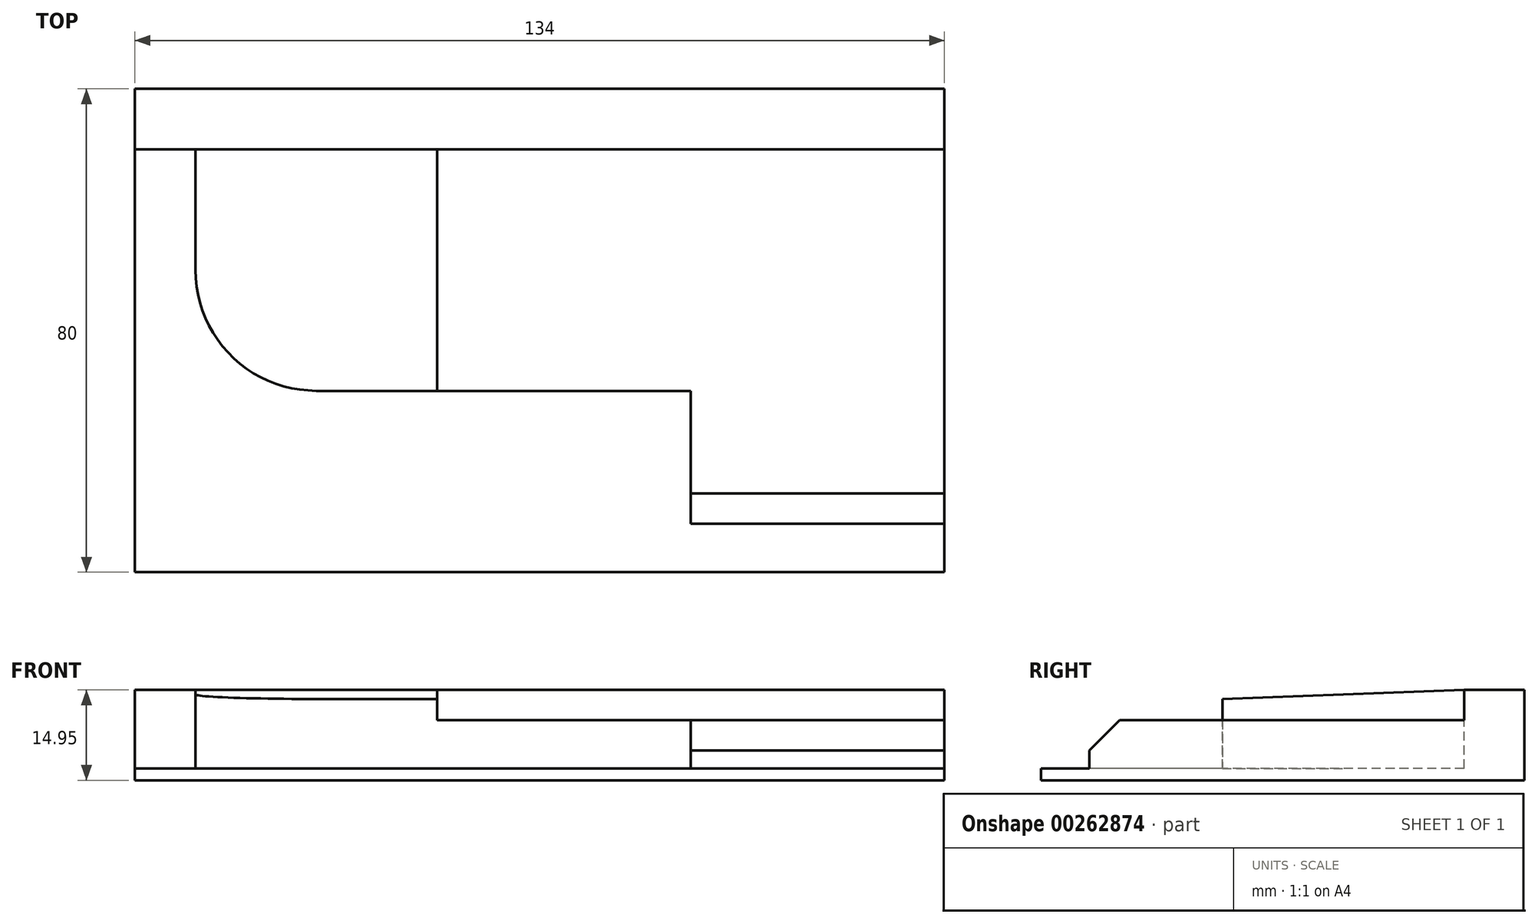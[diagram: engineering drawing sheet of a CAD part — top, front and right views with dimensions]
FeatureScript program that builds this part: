
annotation { "Feature Type Name" : "Feature", "Feature Type Description" : "" }
export const myFeature = defineFeature(function(context is Context, id is Id, definition is map)
    precondition{}
    {
        {
            var Q0;
            Q0=qCreatedBy(makeId("Right.planeOp"),FACE);
            var sketch = newSketch(context, id + "F0", { "sketchPlane" : qUnion([Q0])});
            skLineSegment(sketch, "E0", {"start": v(0, 0) * mm, "end": v(40, 0) * mm});
            skLineSegment(sketch, "E1", {"start": v(0, 0) * mm, "end": v(-40, 0) * mm});
            skLineSegment(sketch, "E2", {"start": v(40, 0) * mm, "end": v(40, 13) * mm});
            skLineSegment(sketch, "E3", {"start": v(40, 13) * mm, "end": v(30, 13) * mm});
            skLineSegment(sketch, "E4", {"start": v(30, 13) * mm, "end": v(30, 8) * mm});
            skLineSegment(sketch, "E5", {"start": v(30, 8) * mm, "end": v(-32, 8) * mm});
            skLineSegment(sketch, "E6", {"start": v(-32, 8) * mm, "end": v(-32, 0) * mm});
            skLineSegment(sketch, "E7", {"start": v(-40, 0) * mm, "end": v(-40, -1.95) * mm});
            skLineSegment(sketch, "E8", {"start": v(-40, -1.95) * mm, "end": v(40, -1.95) * mm});
            skLineSegment(sketch, "E9", {"start": v(40, -1.95) * mm, "end": v(40, 0) * mm});
            skSolve(sketch);
        }
        {
            var Q0;
            {var subQ3=sQuery(id+"F0.wireOp",EDGE,"E0");Q0=makeQuery(id+"F0.imprint","IMPRINT",FACE,{"disambiguationData":[TD([[makeQuery(id+"F0.imprint","IMPRINT",EDGE,{"derivedFrom":subQ3}),-1.0]])]});}
            var Q1;
            {var subQ1=sQuery(id+"F0.wireOp",EDGE,"E0");Q1=makeQuery(id+"F0.imprint","IMPRINT",FACE,{"disambiguationData":[TD([[makeQuery(id+"F0.imprint","IMPRINT",EDGE,{"derivedFrom":subQ1}),1.0]])]});}
            extrude(context, id + "F1", {"entities" : qUnion([Q0, Q1]), "depth" : 42 * mm, "symmetric" : true});
        }
        {
            var Q0;
            Q0=makeQuery(id+"F1.opExtrude","CAP_FACE",FACE,{"disambiguationData":[OSD([sQuery(id+"F0.wireOp",EDGE,"E1"),sQuery(id+"F0.wireOp",EDGE,"E2"),sQuery(id+"F0.wireOp",EDGE,"E3"),sQuery(id+"F0.wireOp",EDGE,"E4"),sQuery(id+"F0.wireOp",EDGE,"E5"),sQuery(id+"F0.wireOp",EDGE,"E6"),sQuery(id+"F0.wireOp",EDGE,"E7"),sQuery(id+"F0.wireOp",EDGE,"E8"),sQuery(id+"F0.wireOp",EDGE,"E9")])],"isStart":true});
            var sketch = newSketch(context, id + "F2", { "sketchPlane" : qUnion([Q0])});
            skLineSegment(sketch, "E10", {"start": v(-40, 13) * mm, "end": v(-40, -1.95) * mm});
            skLineSegment(sketch, "E11", {"start": v(-40, -1.95) * mm, "end": v(40, -1.95) * mm});
            skLineSegment(sketch, "E12", {"start": v(40, -1.95) * mm, "end": v(40, 0) * mm});
            skLineSegment(sketch, "E13", {"start": v(-40, 13) * mm, "end": v(-30, 13) * mm});
            skLineSegment(sketch, "E14", {"start": v(-30, 13) * mm, "end": v(-30, 8) * mm});
            skLineSegment(sketch, "E15", {"start": v(-30, 8) * mm, "end": v(10, 8) * mm});
            skLineSegment(sketch, "E16", {"start": v(10, 8) * mm, "end": v(10, 0) * mm});
            skLineSegment(sketch, "E17", {"start": v(40, 0) * mm, "end": v(10, 0) * mm});
            skSolve(sketch);
        }
        {
            var Q0;
            Q0=makeQuery(id+"F2.imprint","IMPRINT",FACE,{"disambiguationData":[TD([[makeQuery(id+"F2.imprint","IMPRINT",EDGE,{"derivedFrom":sQuery(id+"F2.wireOp",EDGE,"E10")}),-1.0]])]});
            extrude(context, id + "F3", {"entities" : qUnion([Q0]), "operationType" : NewBodyOperationType.ADD, "depth" : 42 * mm});
        }
        {
            var Q0;
            Q0=makeQuery(id+"F3.opExtrude","CAP_FACE",FACE,{"disambiguationData":[OSD([sQuery(id+"F2.wireOp",EDGE,"E10"),sQuery(id+"F2.wireOp",EDGE,"E11"),sQuery(id+"F2.wireOp",EDGE,"E12"),sQuery(id+"F2.wireOp",EDGE,"E13"),sQuery(id+"F2.wireOp",EDGE,"E14"),sQuery(id+"F2.wireOp",EDGE,"E15"),sQuery(id+"F2.wireOp",EDGE,"E16"),sQuery(id+"F2.wireOp",EDGE,"E17")])],"isStart":false});
            var sketch = newSketch(context, id + "F4", { "sketchPlane" : qUnion([Q0])});
            skLineSegment(sketch, "E18", {"start": v(-40, -1.95) * mm, "end": v(40, -1.95) * mm});
            skLineSegment(sketch, "E19", {"start": v(40, -1.95) * mm, "end": v(40, 0) * mm});
            skLineSegment(sketch, "E20", {"start": v(40, 0) * mm, "end": v(-40, 0) * mm});
            skLineSegment(sketch, "E21", {"start": v(-40, 0) * mm, "end": v(-40, -1.95) * mm});
            skSolve(sketch);
        }
        {
            var Q0;
            Q0=makeQuery(id+"F4.imprint","IMPRINT",FACE,{"disambiguationData":[TD([[makeQuery(id+"F4.imprint","IMPRINT",EDGE,{"derivedFrom":sQuery(id+"F4.wireOp",EDGE,"E18")}),-1.0]])]});
            extrude(context, id + "F5", {"entities" : qUnion([Q0]), "operationType" : NewBodyOperationType.ADD, "depth" : 50 * mm});
        }
        {
            var Q0;
            Q0=makeQuery(id+"F3.opExtrude","CAP_FACE",FACE,{"disambiguationData":[OSD([sQuery(id+"F2.wireOp",EDGE,"E10"),sQuery(id+"F2.wireOp",EDGE,"E11"),sQuery(id+"F2.wireOp",EDGE,"E12"),sQuery(id+"F2.wireOp",EDGE,"E13"),sQuery(id+"F2.wireOp",EDGE,"E14"),sQuery(id+"F2.wireOp",EDGE,"E15"),sQuery(id+"F2.wireOp",EDGE,"E16"),sQuery(id+"F2.wireOp",EDGE,"E17")])],"isStart":false});
            var sketch = newSketch(context, id + "F6", { "sketchPlane" : qUnion([Q0])});
            skLineSegment(sketch, "E22", {"start": v(-40, 13) * mm, "end": v(-30, 13) * mm});
            skLineSegment(sketch, "E23", {"start": v(-30, 13) * mm, "end": v(-30, 0) * mm});
            skLineSegment(sketch, "E24", {"start": v(-30, 0) * mm, "end": v(-40, 0) * mm});
            skLineSegment(sketch, "E25", {"start": v(-40, 0) * mm, "end": v(-40, 13) * mm});
            skSolve(sketch);
        }
        {
            var Q0;
            {var subQ3=sQuery(id+"F6.wireOp",EDGE,"E22");Q0=makeQuery(id+"F6.imprint","IMPRINT",FACE,{"disambiguationData":[TD([[makeQuery(id+"F6.imprint","IMPRINT",EDGE,{"derivedFrom":subQ3}),-1.0]])]});}
            extrude(context, id + "F7", {"entities" : qUnion([Q0]), "operationType" : NewBodyOperationType.ADD, "depth" : 50 * mm});
        }
        {
            var Q0;
            Q0=makeQuery(id+"F3.opExtrude","CAP_FACE",FACE,{"disambiguationData":[OSD([sQuery(id+"F2.wireOp",EDGE,"E10"),sQuery(id+"F2.wireOp",EDGE,"E11"),sQuery(id+"F2.wireOp",EDGE,"E12"),sQuery(id+"F2.wireOp",EDGE,"E13"),sQuery(id+"F2.wireOp",EDGE,"E14"),sQuery(id+"F2.wireOp",EDGE,"E15"),sQuery(id+"F2.wireOp",EDGE,"E16"),sQuery(id+"F2.wireOp",EDGE,"E17")])],"isStart":false});
            var sketch = newSketch(context, id + "F8", { "sketchPlane" : qUnion([Q0])});
            skLineSegment(sketch, "E26", {"start": v(-30, 0) * mm, "end": v(10, 0) * mm});
            skLineSegment(sketch, "E27", {"start": v(-30, 0) * mm, "end": v(-30, 13) * mm});
            skLineSegment(sketch, "E28", {"start": v(10, 0) * mm, "end": v(10, 11.5) * mm});
            skLineSegment(sketch, "E29", {"start": v(-30, 13) * mm, "end": v(10, 11.5) * mm});
            skSolve(sketch);
        }
        {
            var Q0;
            {var subQ2=sQuery(id+"F8.wireOp",EDGE,"E29");Q0=makeQuery(id+"F8.imprint","IMPRINT",FACE,{"disambiguationData":[TD([[makeQuery(id+"F8.imprint","IMPRINT",EDGE,{"derivedFrom":subQ2}),-1.0]])]});}
            var Q1;
            {var subQ0=sQuery(id+"F8.wireOp",EDGE,"E26");Q1=makeQuery(id+"F8.imprint","IMPRINT",FACE,{"disambiguationData":[TD([[makeQuery(id+"F8.imprint","IMPRINT",EDGE,{"derivedFrom":subQ0}),1.0]])]});}
            extrude(context, id + "F9", {"entities" : qUnion([Q0, Q1]), "operationType" : NewBodyOperationType.ADD, "depth" : 40 * mm});
        }
        {
            var Q0;
            Q0=makeQuery(id+"F9.opExtrude","CAP_EDGE",EDGE,{"disambiguationData":[OSD([sQuery(id+"F8.wireOp",EDGE,"E28")])],"isStart":false});
            fillet(context, id + "F10", {"entities" : qUnion([Q0]), "radius" : 20 * mm, "tangentPropagation" : true, "allowEdgeOverflow" : false});
        }
        {
            var Q0;
            Q0=makeQuery(id+"F1.opExtrude","SWEPT_EDGE",EDGE,{"disambiguationData":[OSD([sQuery(id+"F0.wireOp",EDGE,"E5"),sQuery(id+"F0.wireOp",EDGE,"E6")])]});
            chamfer(context, id + "F11", {"entities" : qUnion([Q0]), "width" : 5 * mm, "tangentPropagation" : true});
        }
    });
